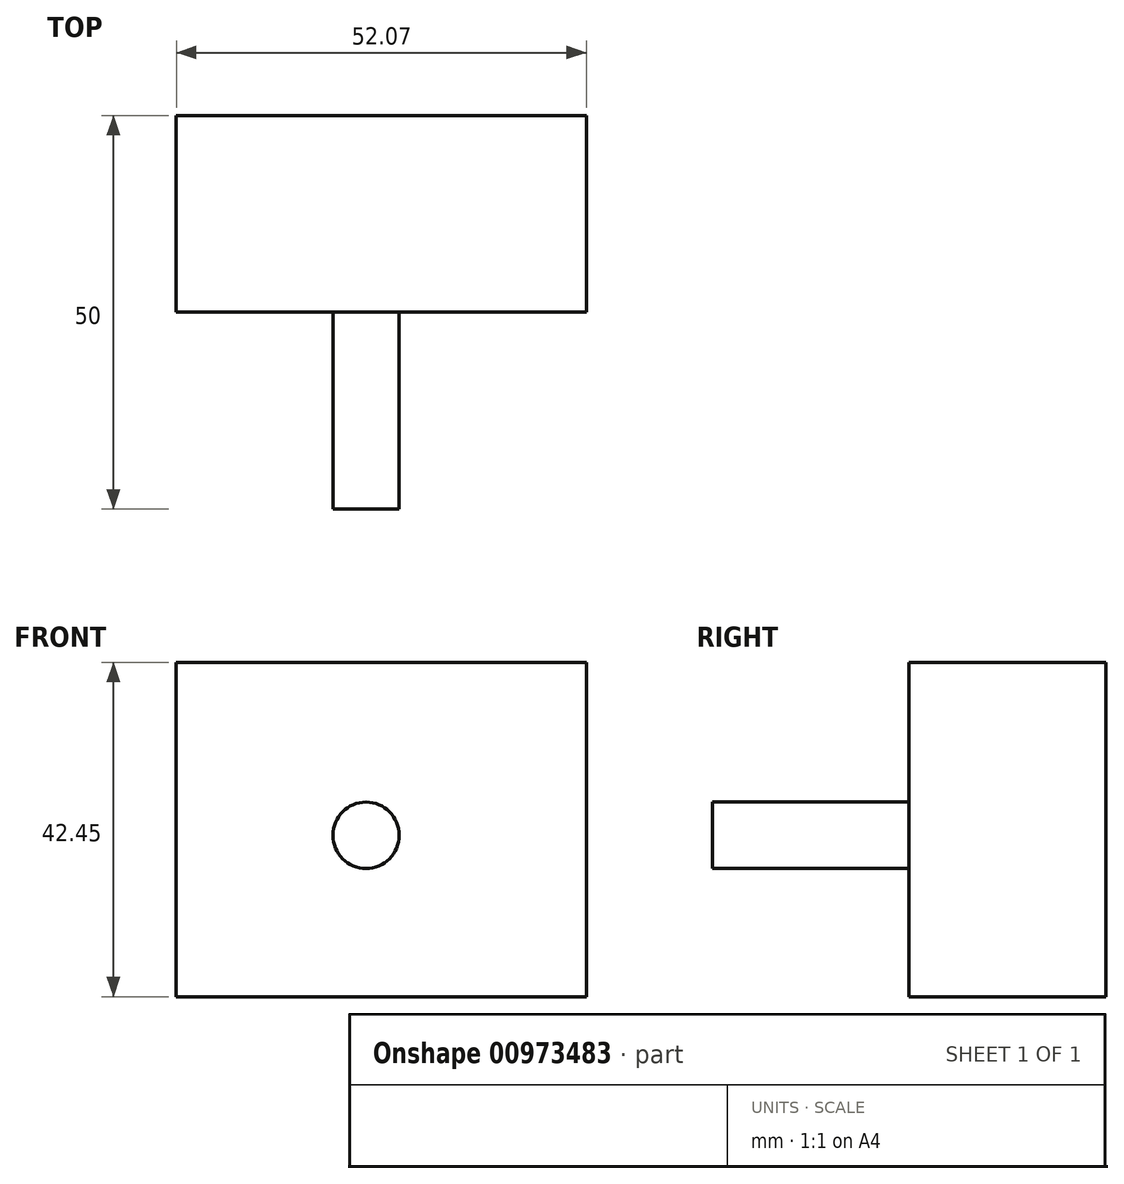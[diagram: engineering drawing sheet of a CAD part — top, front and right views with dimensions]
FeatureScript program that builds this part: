
annotation { "Feature Type Name" : "Feature", "Feature Type Description" : "" }
export const myFeature = defineFeature(function(context is Context, id is Id, definition is map)
    precondition{}
    {
        {
            var Q0;
            Q0=qCreatedBy(makeId("Front.planeOp"),FACE);
            var sketch = newSketch(context, id + "F0", { "sketchPlane" : qUnion([Q0])});
            skLineSegment(sketch, "E0.bottom", {"start": v(-112.65, 0) * mm, "end": v(-60.58, 0) * mm});
            skLineSegment(sketch, "E0.top", {"start": v(-112.65, 42.45) * mm, "end": v(-60.58, 42.45) * mm});
            skLineSegment(sketch, "E0.left", {"start": v(-112.65, 0) * mm, "end": v(-112.65, 42.45) * mm});
            skLineSegment(sketch, "E0.right", {"start": v(-60.58, 0) * mm, "end": v(-60.58, 42.45) * mm});
            skPoint(sketch, "E0.middle", {"position": v(-86.62, 21.23) * mm});
            skSolve(sketch);
        }
        {
            var Q0;
            Q0=makeQuery(id+"F0.imprint","IMPRINT",FACE,{"disambiguationData":[TD([[makeQuery(id+"F0.imprint","IMPRINT",EDGE,{"derivedFrom":sQuery(id+"F0.wireOp",EDGE,"E0.bottom")}),1.0]])]});
            extrude(context, id + "F1", {"entities" : qUnion([Q0]), "depth" : 25 * mm, "offsetDistance" : 25 * mm});
        }
        {
            var Q0;
            Q0=makeQuery(id+"F1.opExtrude","CAP_FACE",FACE,{"disambiguationData":[OSD([sQuery(id+"F0.wireOp",EDGE,"E0.bottom"),sQuery(id+"F0.wireOp",EDGE,"E0.top"),sQuery(id+"F0.wireOp",EDGE,"E0.left"),sQuery(id+"F0.wireOp",EDGE,"E0.right")])],"isStart":false});
            cPlane(context, id + "F2", {"entities" : qUnion([Q0]), "cplaneType" : CPlaneType.OFFSET, "offset" : 25 * mm, "width" : 150 * mm, "height" : 150 * mm});
        }
        {
            var Q0;
            Q0=qCreatedBy(id+"F2.planeOp",FACE);
            var sketch = newSketch(context, id + "F3", { "sketchPlane" : qUnion([Q0])});
            skCircle(sketch, "E1", {"center": v(-88.56, 20.5) * mm, "radius": 4.21 * mm});
            skSolve(sketch);
        }
        {
            var Q0;
            Q0=makeQuery(id+"F3.imprint","IMPRINT",FACE,{"disambiguationData":[TD([[makeQuery(id+"F3.imprint","IMPRINT",EDGE,{"derivedFrom":sQuery(id+"F3.wireOp",EDGE,"E1")}),1.0]])]});
            var Q1;
            Q1=makeQuery(id+"F1.opExtrude","SWEPT_BODY",BODY,{"disambiguationData":[OSD([sQuery(id+"F0.wireOp",EDGE,"E0.bottom"),sQuery(id+"F0.wireOp",EDGE,"E0.top"),sQuery(id+"F0.wireOp",EDGE,"E0.left"),sQuery(id+"F0.wireOp",EDGE,"E0.right")])]});
            extrude(context, id + "F4", {"entities" : qUnion([Q0]), "endBound" : BoundingType.UP_TO_BODY, "oppositeDirection" : true, "depth" : 25 * mm, "endBoundEntityBody" : qUnion([Q1]), "offsetDistance" : 25 * mm});
        }
    });
